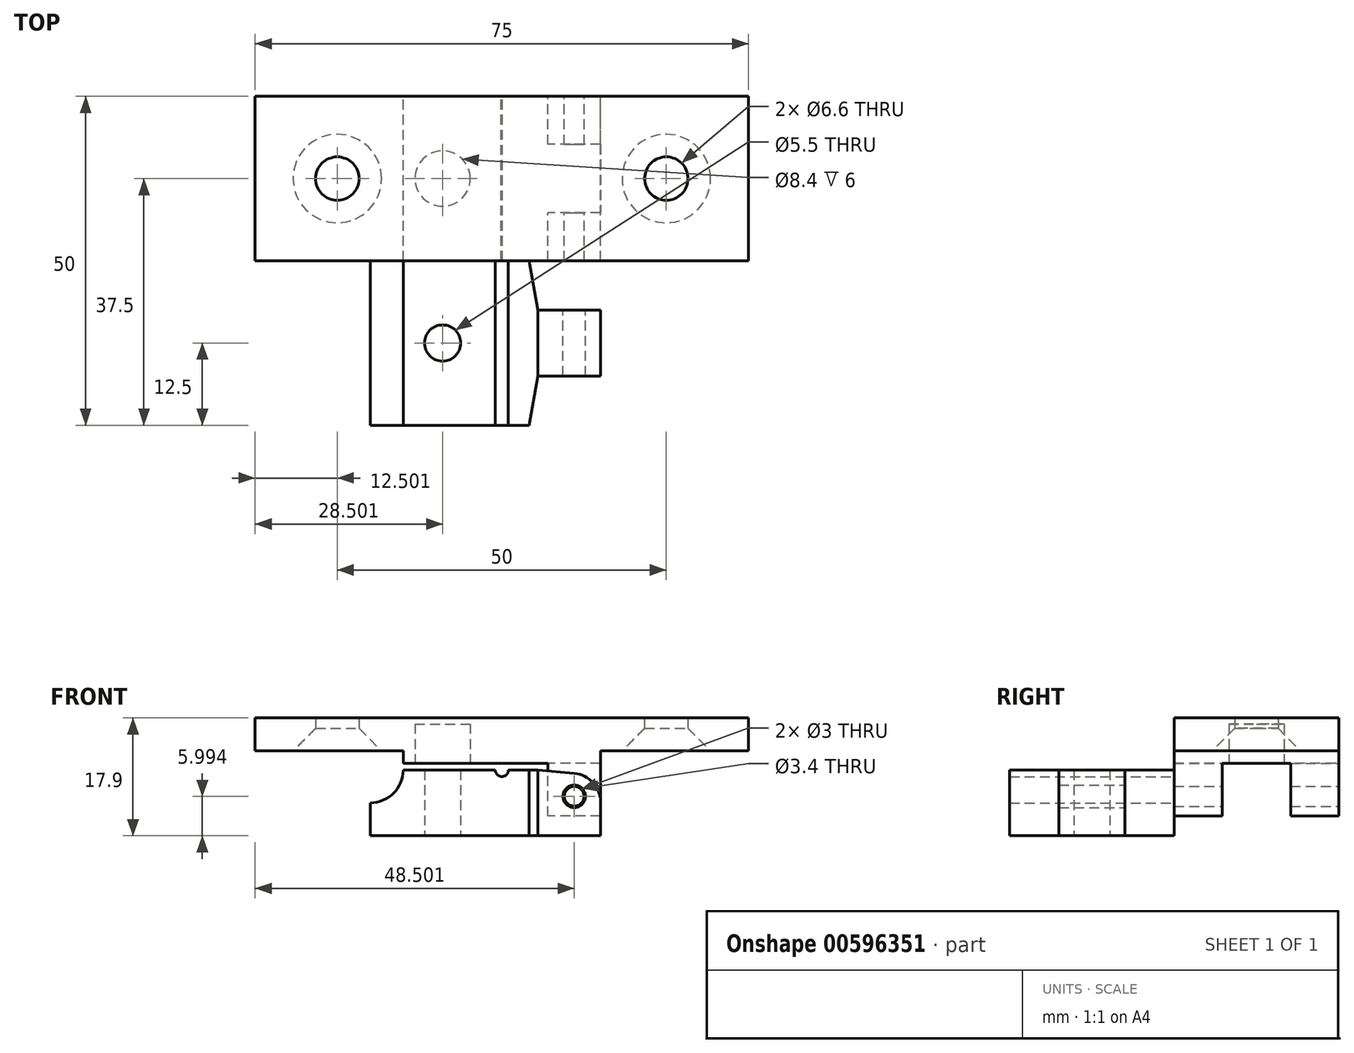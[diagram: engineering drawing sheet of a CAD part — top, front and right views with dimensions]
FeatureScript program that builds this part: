
annotation { "Feature Type Name" : "Feature", "Feature Type Description" : "" }
export const myFeature = defineFeature(function(context is Context, id is Id, definition is map)
    precondition{}
    {
        {
            var Q0;
            Q0=qCreatedBy(makeId("Front.planeOp"),FACE);
            var sketch = newSketch(context, id + "F0", { "sketchPlane" : qUnion([Q0])});
            skLineSegment(sketch, "E0", {"start": v(12.68, -10.49) * mm, "end": v(5.79, -10.49) * mm});
            skLineSegment(sketch, "E1", {"start": v(5.79, -10.49) * mm, "end": v(5.68, -10.38) * mm});
            skLineSegment(sketch, "E2", {"start": v(5.68, -10.38) * mm, "end": v(5.57, -10.49) * mm});
            skLineSegment(sketch, "E3", {"start": v(5.57, -10.49) * mm, "end": v(-9.32, -10.49) * mm});
            skLineSegment(sketch, "E4", {"start": v(-9.32, -10.49) * mm, "end": v(-9.32, -8.58) * mm});
            skLineSegment(sketch, "E5", {"start": v(-9.32, -8.58) * mm, "end": v(20.68, -8.58) * mm});
            skLineSegment(sketch, "E6", {"start": v(20.68, -8.58) * mm, "end": v(20.68, -18.49) * mm});
            skLineSegment(sketch, "E7", {"start": v(20.68, -18.49) * mm, "end": v(12.68, -18.49) * mm});
            skLineSegment(sketch, "E8", {"start": v(12.68, -18.49) * mm, "end": v(12.68, -10.49) * mm});
            skCircle(sketch, "E9", {"center": v(16.68, -15.49) * mm, "radius": 1.5 * mm});
            skLineSegment(sketch, "E10", {"start": v(20.68, -15.49) * mm, "end": v(12.68, -15.49) * mm, "construction": true});
            skSolve(sketch);
        }
        {
            var Q0;
            Q0=qSketchRegion(id+"F0",true);
            extrude(context, id + "F1", {"entities" : qUnion([Q0]), "depth" : 25 * mm, "offsetDistance" : 25 * mm});
        }
        {
            var Q0;
            Q0=makeQuery(id+"F1.opExtrude","SWEPT_FACE",FACE,{"disambiguationData":[OSD([sQuery(id+"F0.wireOp",EDGE,"E3")])]});
            var sketch = newSketch(context, id + "F2", { "sketchPlane" : qUnion([Q0])});
            skCircle(sketch, "E11", {"center": v(-3.32, 12.5) * mm, "radius": 4.2 * mm});
            skLineSegment(sketch, "E12", {"start": v(-3.32, 25) * mm, "end": v(-3.32, 0) * mm, "construction": true});
            skSolve(sketch);
        }
        {
            var Q0;
            Q0=makeQuery(id+"F1.opExtrude","SWEPT_FACE",FACE,{"disambiguationData":[OSD([sQuery(id+"F0.wireOp",EDGE,"E5")])]});
            var sketch = newSketch(context, id + "F3", { "sketchPlane" : qUnion([Q0])});
            skLineSegment(sketch, "E13.bottom", {"start": v(-31.82, -25) * mm, "end": v(43.18, -25) * mm});
            skLineSegment(sketch, "E13.top", {"start": v(-31.82, 0) * mm, "end": v(43.18, 0) * mm});
            skLineSegment(sketch, "E13.left", {"start": v(-31.82, -25) * mm, "end": v(-31.82, 0) * mm});
            skLineSegment(sketch, "E13.right", {"start": v(43.18, -25) * mm, "end": v(43.18, 0) * mm});
            skPoint(sketch, "E14", {"position": v(5.68, 0) * mm});
            skLineSegment(sketch, "E15", {"start": v(30.68, 0) * mm, "end": v(30.68, -25) * mm, "construction": true});
            skLineSegment(sketch, "E16", {"start": v(-19.32, -12.5) * mm, "end": v(30.68, -12.5) * mm, "construction": true});
            skPoint(sketch, "E17", {"position": v(30.68, -12.5) * mm});
            skPoint(sketch, "E18", {"position": v(-19.32, -12.5) * mm});
            skSolve(sketch);
        }
        {
            var Q0;
            Q0=qSketchRegion(id+"F3",true);
            extrude(context, id + "F4", {"entities" : qUnion([Q0]), "operationType" : NewBodyOperationType.ADD, "depth" : 5 * mm, "offsetDistance" : 25 * mm});
        }
        {
            var Q0;
            Q0=qSketchRegion(id+"F2",true);
            extrude(context, id + "F5", {"entities" : qUnion([Q0]), "operationType" : NewBodyOperationType.REMOVE, "oppositeDirection" : true, "depth" : 6 * mm, "offsetDistance" : 25 * mm});
        }
        {
            var Q0;
            Q0=sQuery(id+"F3.wireOp",VERTEX,"E17");
            var Q1;
            Q1=sQuery(id+"F3.wireOp",VERTEX,"E18");
            var Q2;
            Q2=makeQuery(id+"F1.opExtrude","SWEPT_BODY",BODY,{"disambiguationData":[OSD([sQuery(id+"F0.wireOp",EDGE,"E0"),sQuery(id+"F0.wireOp",EDGE,"E1"),sQuery(id+"F0.wireOp",EDGE,"fda18a35-4a45-4902-97d1-b4d1b1f57ba1"),sQuery(id+"F0.wireOp",EDGE,"E2"),sQuery(id+"F0.wireOp",EDGE,"E3"),sQuery(id+"F0.wireOp",EDGE,"E4"),sQuery(id+"F0.wireOp",EDGE,"E5"),sQuery(id+"F0.wireOp",EDGE,"E6"),sQuery(id+"F0.wireOp",EDGE,"E7"),sQuery(id+"F0.wireOp",EDGE,"E8"),sQuery(id+"F0.wireOp",EDGE,"E9")])]});
            hole(context, id + "F6", {"style" : HoleStyle.C_SINK, "endStyle" : HoleEndStyle.THROUGH, "oppositeDirection" : true, "standardTappedOrClearance" : lookupTablePath({ "standard" : "ISO", "fit" : "Normal", "size" : "M6", "type" : "Clearance" }), "standardBlindInLast" : lookupTablePath({ "fit" : "Standard", "standard" : "ISO", "size" : "M6", "type" : "Clearance" }), "holeDiameter" : 6.6 * mm, "cSinkDiameter" : 13.44 * mm, "cSinkAngle" : 90 * degree, "majorDiameter" : 5 * mm, "isTappedThrough" : true, "tappedDepth" : 12 * mm, "tapClearance" : 3, "locations" : qUnion([Q0, Q1]), "scope" : qUnion([Q2])});
        }
        {
            var Q0;
            Q0=makeQuery(id+"F1.opExtrude","SWEPT_FACE",FACE,{"disambiguationData":[OSD([sQuery(id+"F0.wireOp",EDGE,"E8")])]});
            var sketch = newSketch(context, id + "F7", { "sketchPlane" : qUnion([Q0])});
            skLineSegment(sketch, "E19.bottom", {"start": v(7.3, -18.49) * mm, "end": v(17.7, -18.49) * mm});
            skLineSegment(sketch, "E19.top", {"start": v(7.3, -10.49) * mm, "end": v(17.7, -10.49) * mm});
            skLineSegment(sketch, "E19.left", {"start": v(7.3, -18.49) * mm, "end": v(7.3, -10.49) * mm});
            skLineSegment(sketch, "E19.right", {"start": v(17.7, -18.49) * mm, "end": v(17.7, -10.49) * mm});
            skSolve(sketch);
        }
        {
            var Q0;
            Q0=qSketchRegion(id+"F7",true);
            extrude(context, id + "F8", {"entities" : qUnion([Q0]), "operationType" : NewBodyOperationType.REMOVE, "oppositeDirection" : true, "depth" : 25 * mm, "offsetDistance" : 25 * mm});
        }
        {
            var Q0;
            Q0=makeQuery(id+"F4.boolean.opBoolean","MERGE",FACE,{"derivedFrom":[makeQuery(id+"F1.opExtrude","CAP_FACE",FACE,{"disambiguationData":[OSD([sQuery(id+"F0.wireOp",EDGE,"E0"),sQuery(id+"F0.wireOp",EDGE,"E1"),sQuery(id+"F0.wireOp",EDGE,"fda18a35-4a45-4902-97d1-b4d1b1f57ba1"),sQuery(id+"F0.wireOp",EDGE,"E2"),sQuery(id+"F0.wireOp",EDGE,"E3"),sQuery(id+"F0.wireOp",EDGE,"E4"),sQuery(id+"F0.wireOp",EDGE,"E5"),sQuery(id+"F0.wireOp",EDGE,"E6"),sQuery(id+"F0.wireOp",EDGE,"E7"),sQuery(id+"F0.wireOp",EDGE,"E8"),sQuery(id+"F0.wireOp",EDGE,"E9")])],"isStart":false}),makeQuery(id+"F4.opExtrude","SWEPT_FACE",FACE,{"disambiguationData":[OSD([sQuery(id+"F3.wireOp",EDGE,"E13.bottom")])]})]});
            var sketch = newSketch(context, id + "F9", { "sketchPlane" : qUnion([Q0])});
            skArc(sketch, "E20", {"start": v(4.68, -11.48) * mm, "mid": v(5.68, -12.48) * mm, "end": v(6.68, -11.48) * mm});
            skLineSegment(sketch, "E21", {"start": v(4.68, -11.48) * mm, "end": v(-9.32, -11.48) * mm});
            skArc(sketch, "E22", {"start": v(-14.32, -16.48) * mm, "mid": v(-10.78, -15.02) * mm, "end": v(-9.32, -11.48) * mm});
            skLineSegment(sketch, "E23", {"start": v(-14.32, -16.48) * mm, "end": v(-14.32, -21.48) * mm});
            skLineSegment(sketch, "E24", {"start": v(-14.32, -21.48) * mm, "end": v(20.68, -21.48) * mm});
            skCircle(sketch, "E25", {"center": v(5.68, -11.48) * mm, "radius": 1 * mm, "construction": true});
            skPoint(sketch, "E26", {"position": v(5.68, -10.38) * mm});
            skLineSegment(sketch, "E27", {"start": v(5.68, -11.48) * mm, "end": v(5.68, -10.38) * mm, "construction": true});
            skPoint(sketch, "E28", {"position": v(-4.32, -21.48) * mm});
            skLineSegment(sketch, "E29", {"start": v(-9.32, -21.48) * mm, "end": v(-9.32, -11.48) * mm, "construction": true});
            skCircle(sketch, "E30", {"center": v(16.68, -15.49) * mm, "radius": 1.7 * mm});
            skLineSegment(sketch, "E31", {"start": v(20.68, -21.48) * mm, "end": v(20.68, -16.37) * mm});
            skLineSegment(sketch, "E32", {"start": v(11.18, -11.48) * mm, "end": v(6.68, -11.48) * mm});
            skLineSegment(sketch, "E33", {"start": v(11.18, -11.48) * mm, "end": v(16.68, -11.99) * mm});
            skArc(sketch, "E34", {"start": v(20.68, -16.37) * mm, "mid": v(19.53, -13.4) * mm, "end": v(16.68, -11.99) * mm});
            skSolve(sketch);
        }
        {
            var Q0;
            Q0=qSketchRegion(id+"F9",true);
            extrude(context, id + "F10", {"entities" : qUnion([Q0]), "depth" : 25 * mm, "offsetDistance" : 25 * mm});
        }
        {
            var Q0;
            Q0=makeQuery(id+"F10.opExtrude","SWEPT_FACE",FACE,{"disambiguationData":[OSD([sQuery(id+"F9.wireOp",EDGE,"E24")])]});
            var sketch = newSketch(context, id + "F11", { "sketchPlane" : qUnion([Q0])});
            skLineSegment(sketch, "E35", {"start": v(-3.32, 55.83) * mm, "end": v(-3.32, 19.17) * mm, "construction": true});
            skPoint(sketch, "E36", {"position": v(-3.32, 37.5) * mm});
            skSolve(sketch);
        }
        {
            var Q0;
            Q0=sQuery(id+"F11.wireOp",VERTEX,"E36");
            var Q1;
            Q1=makeQuery(id+"F10.opExtrude","SWEPT_BODY",BODY,{"disambiguationData":[OSD([sQuery(id+"F9.wireOp",EDGE,"NBDfFKbi-qGs6-JKBK-J2hD-w34obwZNQX4o"),sQuery(id+"F9.wireOp",EDGE,"E20"),sQuery(id+"F9.wireOp",EDGE,"E21"),sQuery(id+"F9.wireOp",EDGE,"E22"),sQuery(id+"F9.wireOp",EDGE,"E23"),sQuery(id+"F9.wireOp",EDGE,"E24"),sQuery(id+"F9.wireOp",EDGE,"Cpo2Mnzs-FqZ4-VE5m-oe0K-q216ubIeRApR"),sQuery(id+"F9.wireOp",EDGE,"4pz4DvDe-8K02-BGV1-GMiS-25PLyMDL3cYd"),sQuery(id+"F9.wireOp",EDGE,"RzoUX08u-rRmn-cew6-mJfb-Ws3PqcxDGY6H")])]});
            hole(context, id + "F12", {"style" : HoleStyle.SIMPLE, "endStyle" : HoleEndStyle.THROUGH, "standardTappedOrClearance" : lookupTablePath({ "standard" : "ISO", "engagement" : "50%", "pitch" : "0.75 mm", "size" : "M6", "type" : "Tapped" }), "standardBlindInLast" : lookupTablePath({ "standard" : "ISO", "engagement" : "50%", "pitch" : "0.75 mm", "size" : "M6", "type" : "Tapped" }), "holeDiameter" : 5.5 * mm, "majorDiameter" : 6 * mm, "showTappedDepth" : true, "isTappedThrough" : true, "tappedDepth" : 12 * mm, "tapClearance" : 3, "locations" : qUnion([Q0]), "scope" : qUnion([Q1])});
        }
        {
            var Q0;
            Q0=makeQuery(id+"F10.opExtrude","SWEPT_FACE",FACE,{"disambiguationData":[OSD([sQuery(id+"F9.wireOp",EDGE,"E32")])]});
            var sketch = newSketch(context, id + "F13", { "sketchPlane" : qUnion([Q0])});
            skLineSegment(sketch, "E37.bottom", {"start": v(9.86, -25) * mm, "end": v(39.86, -25) * mm});
            skLineSegment(sketch, "E37.left", {"start": v(9.86, -25) * mm, "end": v(9.86, -25) * mm});
            skLineSegment(sketch, "E37.right", {"start": v(39.86, -25) * mm, "end": v(39.86, -32.5) * mm});
            skLineSegment(sketch, "E38", {"start": v(6.68, -37.5) * mm, "end": v(22.28, -37.5) * mm, "construction": true});
            skLineSegment(sketch, "E39", {"start": v(9.86, -25) * mm, "end": v(11.18, -32.5) * mm});
            skLineSegment(sketch, "E40", {"start": v(11.18, -32.5) * mm, "end": v(39.86, -32.5) * mm});
            skLineSegment(sketch, "E41.MirrorCS", {"start": v(9.86, -50) * mm, "end": v(11.18, -42.5) * mm});
            skLineSegment(sketch, "E42.MirrorCS", {"start": v(11.18, -42.5) * mm, "end": v(39.86, -42.5) * mm});
            skLineSegment(sketch, "E43.MirrorCS", {"start": v(39.86, -50) * mm, "end": v(39.86, -42.5) * mm});
            skLineSegment(sketch, "E44.MirrorCS", {"start": v(9.86, -50) * mm, "end": v(39.86, -50) * mm});
            skSolve(sketch);
        }
        {
            var Q0;
            Q0 = qSketchRegion(id + "F13", true);
            extrude(context, id + "F14", {"entities" : qUnion([Q0]), "operationType" : NewBodyOperationType.REMOVE, "endBound" : BoundingType.THROUGH_ALL, "oppositeDirection" : true, "depth" : 25 * mm, "offsetDistance" : 25 * mm});
        }
    });
